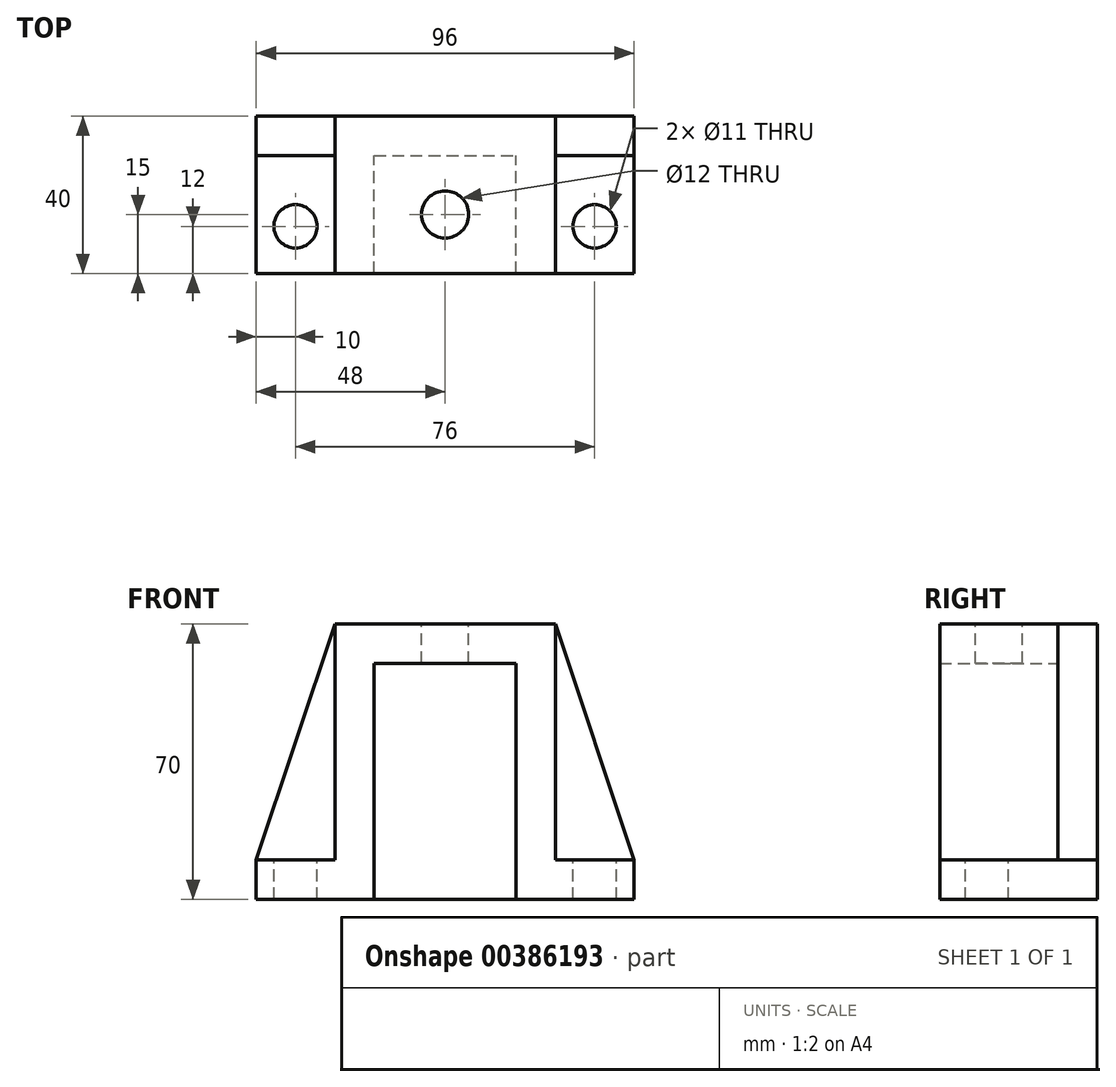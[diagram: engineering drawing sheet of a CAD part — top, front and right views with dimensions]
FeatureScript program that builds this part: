
annotation { "Feature Type Name" : "Feature", "Feature Type Description" : "" }
export const myFeature = defineFeature(function(context is Context, id is Id, definition is map)
    precondition{}
    {
        {
            var Q0;
            Q0=qCreatedBy(makeId("Front.planeOp"),FACE);
            var sketch = newSketch(context, id + "F0", { "sketchPlane" : qUnion([Q0])});
            skLineSegment(sketch, "E0.bottom", {"start": v(-31.5, 48.33) * mm, "end": v(24.5, 48.33) * mm});
            skLineSegment(sketch, "E0.top", {"start": v(-51.5, -21.67) * mm, "end": v(-21.5, -21.67) * mm});
            skLineSegment(sketch, "E0.right", {"start": v(44.5, -11.67) * mm, "end": v(44.5, -21.67) * mm});
            skLineSegment(sketch, "E1.right", {"start": v(-21.5, -21.67) * mm, "end": v(-21.5, 38.33) * mm});
            skLineSegment(sketch, "E2", {"start": v(-31.5, -11.67) * mm, "end": v(-31.5, 48.33) * mm});
            skLineSegment(sketch, "E3", {"start": v(-31.5, 48.33) * mm, "end": v(-51.5, -11.67) * mm});
            skLineSegment(sketch, "E4", {"start": v(-51.5, -11.67) * mm, "end": v(-31.5, -11.67) * mm});
            skLineSegment(sketch, "E5", {"start": v(-51.5, -11.67) * mm, "end": v(-51.5, -21.67) * mm});
            skLineSegment(sketch, "E6.left", {"start": v(44.5, -21.67) * mm, "end": v(44.5, -11.67) * mm});
            skLineSegment(sketch, "E6.right", {"start": v(14.5, -21.67) * mm, "end": v(14.5, 38.33) * mm});
            skLineSegment(sketch, "E7", {"start": v(-21.5, 38.33) * mm, "end": v(14.5, 38.33) * mm});
            skLineSegment(sketch, "E8.bottom", {"start": v(44.5, -11.67) * mm, "end": v(24.5, -11.67) * mm});
            skLineSegment(sketch, "E9.trimOffspring", {"start": v(14.5, -21.67) * mm, "end": v(44.5, -21.67) * mm});
            skLineSegment(sketch, "E10", {"start": v(-21.5, -21.67) * mm, "end": v(14.5, -21.67) * mm});
            skLineSegment(sketch, "E11", {"start": v(24.5, -11.67) * mm, "end": v(24.5, 48.33) * mm});
            skLineSegment(sketch, "E12", {"start": v(24.5, 48.33) * mm, "end": v(44.5, -11.67) * mm});
            skSolve(sketch);
        }
        {
            var Q0;
            Q0=makeQuery(id+"F0.imprint","IMPRINT",FACE,{"disambiguationData":[TD([[makeQuery(id+"F0.imprint","IMPRINT",EDGE,{"derivedFrom":sQuery(id+"F0.wireOp",EDGE,"E0.bottom")}),-1.0]])]});
            extrude(context, id + "F1", {"entities" : qUnion([Q0]), "depth" : 40 * mm});
        }
        {
            var Q0;
            Q0 = qSketchRegion(id + "F0", true);
            extrude(context, id + "F2", {"entities" : qUnion([Q0]), "operationType" : NewBodyOperationType.ADD, "depth" : 10 * mm});
        }
        {
            var Q0;
            Q0=makeQuery(id+"F1.opExtrude","SWEPT_FACE",FACE,{"disambiguationData":[OSD([sQuery(id+"F0.wireOp",EDGE,"E0.bottom")])]});
            var sketch = newSketch(context, id + "F3", { "sketchPlane" : qUnion([Q0])});
            skCircle(sketch, "E13", {"center": v(-3.5, -25) * mm, "radius": 6 * mm});
            skSolve(sketch);
        }
        {
            var Q0;
            Q0 = qSketchRegion(id + "F3", true);
            extrude(context, id + "F4", {"entities" : qUnion([Q0]), "operationType" : NewBodyOperationType.REMOVE, "oppositeDirection" : true, "depth" : 25 * mm});
        }
        {
            var Q0;
            Q0=makeQuery(id+"F1.opExtrude","SWEPT_FACE",FACE,{"disambiguationData":[OSD([sQuery(id+"F0.wireOp",EDGE,"E0.bottom")])]});
            var sketch = newSketch(context, id + "F5", { "sketchPlane" : qUnion([Q0])});
            skCircle(sketch, "E14", {"center": v(-41.5, -28) * mm, "radius": 5.5 * mm});
            skCircle(sketch, "E15", {"center": v(34.5, -28) * mm, "radius": 5.5 * mm});
            skSolve(sketch);
        }
        {
            var Q0;
            Q0 = qSketchRegion(id + "F5", true);
            extrude(context, id + "F6", {"entities" : qUnion([Q0]), "operationType" : NewBodyOperationType.REMOVE, "oppositeDirection" : true, "depth" : 250 * mm});
        }
    });
